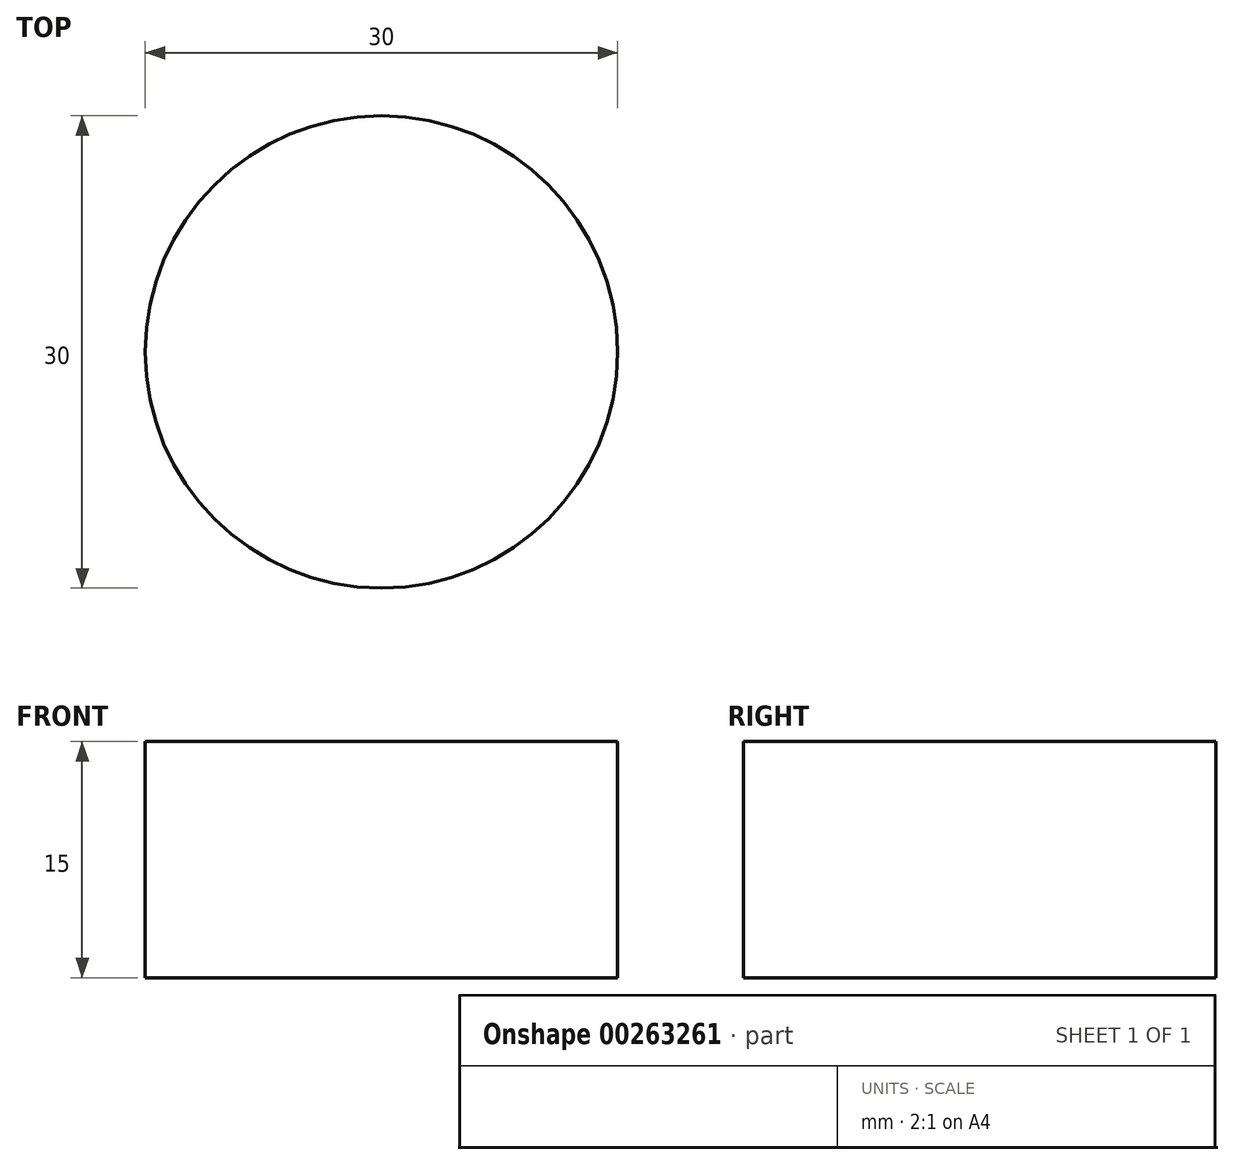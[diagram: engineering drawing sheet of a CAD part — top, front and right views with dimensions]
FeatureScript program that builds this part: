
annotation { "Feature Type Name" : "Feature", "Feature Type Description" : "" }
export const myFeature = defineFeature(function(context is Context, id is Id, definition is map)
    precondition{}
    {
        {
            var Q0;
            Q0=qCreatedBy(makeId("Top.planeOp"),FACE);
            var sketch = newSketch(context, id + "F0", { "sketchPlane" : qUnion([Q0])});
            skCircle(sketch, "E0", {"center": v(0, 0) * mm, "radius": 15 * mm});
            skSolve(sketch);
        }
        {
            var Q0;
            Q0 = qSketchRegion(id + "F0", true);
            extrude(context, id + "F1", {"entities" : qUnion([Q0]), "depth" : 15 * mm});
        }
    });
